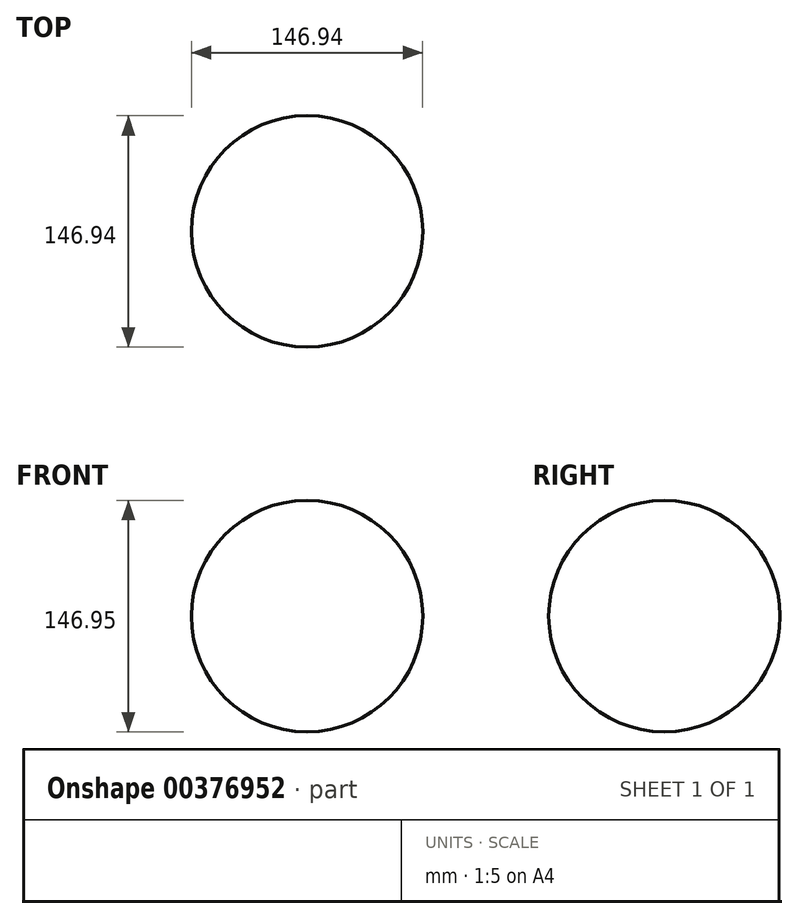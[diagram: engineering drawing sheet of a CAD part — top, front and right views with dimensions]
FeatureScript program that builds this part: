
annotation { "Feature Type Name" : "Feature", "Feature Type Description" : "" }
export const myFeature = defineFeature(function(context is Context, id is Id, definition is map)
    precondition{}
    {
        {
            var Q0;
            Q0=qCreatedBy(makeId("Front.planeOp"),FACE);
            var sketch = newSketch(context, id + "F0", { "sketchPlane" : qUnion([Q0])});
            skArc(sketch, "E0", {"start": v(-106.04, 153.49) * mm, "mid": v(-179.51, 80.01) * mm, "end": v(-106.04, 6.54) * mm});
            skLineSegment(sketch, "E1", {"start": v(-106.04, 80.01) * mm, "end": v(-106.04, 153.49) * mm});
            skLineSegment(sketch, "E2", {"start": v(-106.04, 153.49) * mm, "end": v(-106.04, 6.54) * mm});
            skSolve(sketch);
        }
        {
            var Q0;
            {var subQ0=sQuery(id+"F0.wireOp",EDGE,"E0");Q0=makeQuery(id+"F0.imprint","IMPRINT",FACE,{"disambiguationData":[TD([[makeQuery(id+"F0.imprint","IMPRINT",EDGE,{"derivedFrom":subQ0}),1.0]])]});}
            var Q1;
            Q1=sQuery(id+"F0.wireOp",EDGE,"E2");
            revolve(context, id + "F1", {"entities" : qUnion([Q0]), "axis" : qUnion([Q1]), "revolveType" : RevolveType.FULL});
        }
    });
